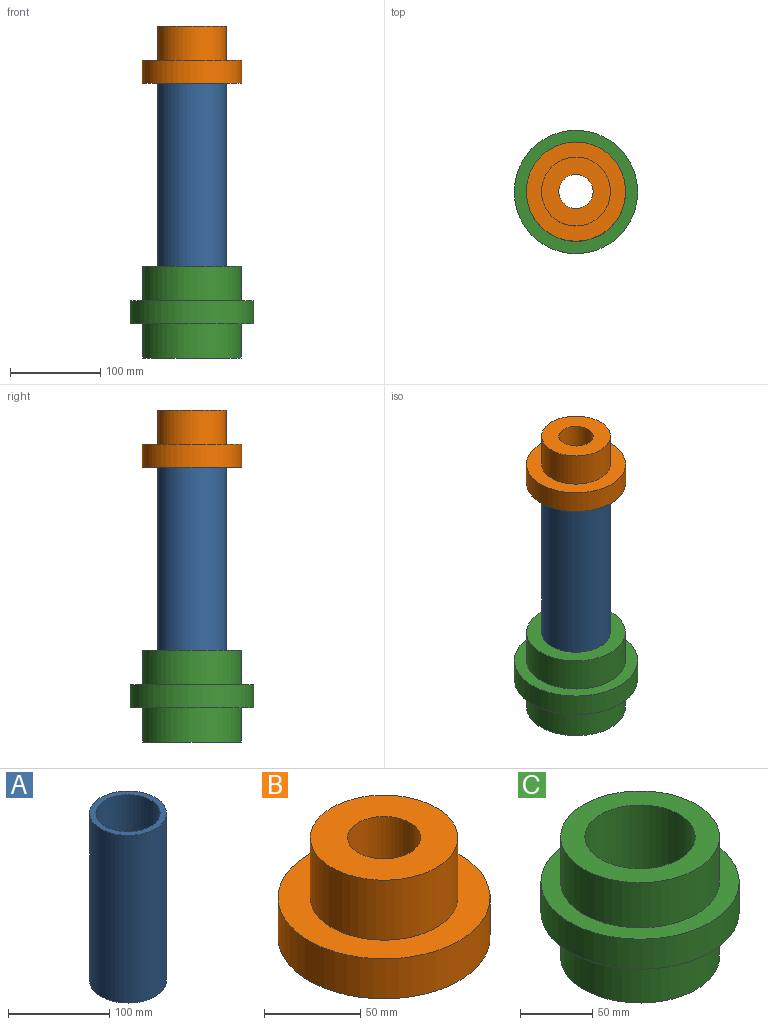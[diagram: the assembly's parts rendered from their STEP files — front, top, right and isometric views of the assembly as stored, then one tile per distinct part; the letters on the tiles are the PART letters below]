
ASSEMBLY  parts=3 mates=2
PART A: 4 faces, bbox 76.2x76.2x203.2 mm
  f0: cylinder r=31.75mm len=203.2mm, axis (0,0,-1), area 40536.6mm2, adj f2,f3
  f1: cylinder r=38.1mm len=203.2mm, axis (0,0,-1), area 48643.9mm2, adj f2,f3
  f2: plane 76.2x76.2mm, normal (0,0,1), area 1393.4mm2, adj f0,f1
  f3: plane 76.2x76.2mm, normal (0,0,-1), area 1393.4mm2, adj f0,f1
PART B: 6 faces, bbox 110.1x110.1x63.5 mm
  f0: cylinder r=55.03mm len=110.07mm, axis (0,0,-1), area 8783.1mm2, adj f1,f2
  f1: plane 110.07x110.07mm, normal (0,0,1), area 4923.1mm2, adj f0,f4
  f2: plane 110.07x110.07mm, normal (0,0,-1), area 8379.9mm2, adj f0,f3
  f3: cylinder r=19.01mm len=63.5mm, axis (0,0,-1), area 7584.3mm2, adj f2,f5
  f4: cylinder r=38.23mm len=76.46mm, axis (0,0,-1), area 9152.3mm2, adj f1,f5
  f5: plane 76.46x76.46mm, normal (0,0,1), area 3456.8mm2, adj f3,f4
PART C: 8 faces, bbox 136.8x136.8x101.6 mm
  f0: cylinder r=38.1mm len=101.6mm, axis (0,0,-1), area 24322mm2, adj f2,f7
  f1: cylinder r=54.84mm len=109.69mm, axis (0,0,-1), area 13129.2mm2, adj f2,f4
  f2: plane 109.69x109.69mm, normal (0,0,1), area 4889.2mm2, adj f0,f1
  f3: cylinder r=68.41mm len=136.83mm, axis (0,0,-1), area 10918.4mm2, adj f4,f5
  f4: plane 136.83x136.83mm, normal (0,0,1), area 5254.6mm2, adj f1,f3
  f5: plane 136.83x136.83mm, normal (0,0,-1), area 5254.6mm2, adj f3,f6
  f6: cylinder r=54.84mm len=109.69mm, axis (0,0,1), area 13129.2mm2, adj f5,f7
  f7: plane 109.69x109.69mm, normal (0,0,-1), area 4889.2mm2, adj f0,f6
PLACE A t=(-24.51,-17.83,-107.12)mm
PLACE B t=(-24.51,-17.83,96.08)mm
PLACE C t=(-24.51,-17.83,-157.92)mm
MATE fastened B.f0 <-> A.f0  axis (0,0,-1) through (-24.51,-17.83,96.08)mm
MATE fastened C.f3 <-> A.f0  axis (0,0,1) through (-24.51,-17.83,-107.12)mm
